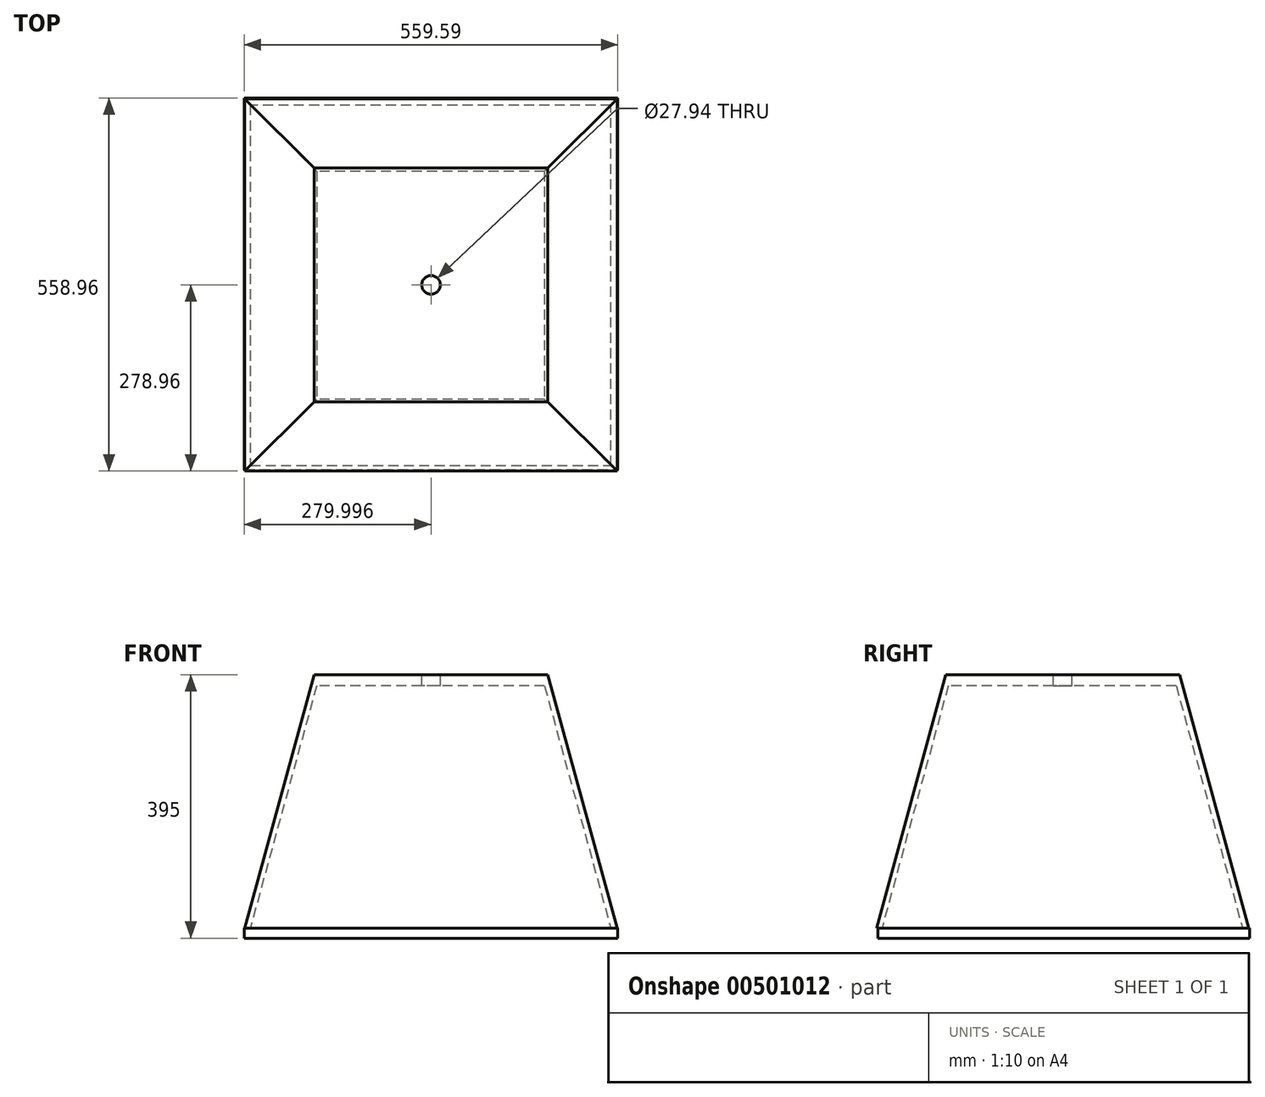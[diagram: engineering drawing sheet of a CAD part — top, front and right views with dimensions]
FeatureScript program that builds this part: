
annotation { "Feature Type Name" : "Feature", "Feature Type Description" : "" }
export const myFeature = defineFeature(function(context is Context, id is Id, definition is map)
    precondition{}
    {
        {
            var Q0;
            Q0=qCreatedBy(makeId("Right.planeOp"),FACE);
            var sketch = newSketch(context, id + "F0", { "sketchPlane" : qUnion([Q0])});
            skLineSegment(sketch, "E0.bottom", {"start": v(0, 0) * mm, "end": v(-560, 0) * mm});
            skLineSegment(sketch, "E0.top", {"start": v(0, -560) * mm, "end": v(-560, -560) * mm});
            skLineSegment(sketch, "E0.left", {"start": v(0, 0) * mm, "end": v(0, -560) * mm});
            skLineSegment(sketch, "E0.right", {"start": v(-560, 0) * mm, "end": v(-560, -560) * mm});
            skSolve(sketch);
        }
        {
            var Q0;
            Q0=qSketchRegion(id+"F0",true);
            var Q1;
            Q1=makeQuery(id+"F0.imprint","IMPRINT",FACE,{"disambiguationData":[TD([[makeQuery(id+"F0.imprint","IMPRINT",EDGE,{"derivedFrom":sQuery(id+"F0.wireOp",EDGE,"E0.bottom")}),1.0]])]});
            extrude(context, id + "F1", {"entities" : qUnion([Q0, Q1]), "depth" : 380 * mm});
        }
        {
            var Q0;
            Q0=makeQuery(id+"F1.opExtrude","CAP_EDGE",EDGE,{"disambiguationData":[OSD([sQuery(id+"F0.wireOp",EDGE,"E0.top")])],"isStart":false});
            chamfer(context, id + "F2", {"entities" : qUnion([Q0]), "chamferType" : ChamferType.OFFSET_ANGLE, "width" : 105 * mm, "oppositeDirection" : true, "angle" : 74.7 * degree, "tangentPropagation" : true});
        }
        {
            var Q0;
            Q0=makeQuery(id+"F1.opExtrude","CAP_EDGE",EDGE,{"disambiguationData":[OSD([sQuery(id+"F0.wireOp",EDGE,"E0.bottom")])],"isStart":false});
            chamfer(context, id + "F3", {"entities" : qUnion([Q0]), "chamferType" : ChamferType.OFFSET_ANGLE, "width" : 105 * mm, "oppositeDirection" : false, "angle" : 74.7 * degree, "tangentPropagation" : true});
        }
        {
            var Q0;
            Q0=makeQuery(id+"F1.opExtrude","CAP_EDGE",EDGE,{"disambiguationData":[OSD([sQuery(id+"F0.wireOp",EDGE,"E0.right")])],"isStart":false});
            chamfer(context, id + "F4", {"entities" : qUnion([Q0]), "chamferType" : ChamferType.OFFSET_ANGLE, "width" : 105 * mm, "oppositeDirection" : false, "angle" : 74.7 * degree, "tangentPropagation" : true});
        }
        {
            var Q0;
            Q0=makeQuery(id+"F1.opExtrude","CAP_EDGE",EDGE,{"disambiguationData":[OSD([sQuery(id+"F0.wireOp",EDGE,"E0.left")])],"isStart":false});
            chamfer(context, id + "F5", {"entities" : qUnion([Q0]), "chamferType" : ChamferType.OFFSET_ANGLE, "width" : 105 * mm, "oppositeDirection" : true, "angle" : 74.7 * degree, "tangentPropagation" : true});
        }
        {
            var Q0;
            Q0=makeQuery(id+"F1.opExtrude","CAP_FACE",FACE,{"disambiguationData":[OSD([sQuery(id+"F0.wireOp",EDGE,"E0.bottom"),sQuery(id+"F0.wireOp",EDGE,"E0.top"),sQuery(id+"F0.wireOp",EDGE,"E0.left"),sQuery(id+"F0.wireOp",EDGE,"E0.right")])],"isStart":false});
            var sketch = newSketch(context, id + "F6", { "sketchPlane" : qUnion([Q0])});
            skLineSegment(sketch, "E1", {"start": v(-105, -455) * mm, "end": v(-455, -455) * mm});
            skCircle(sketch, "E2", {"center": v(-280, -280) * mm, "radius": 13.97 * mm});
            skPoint(sketch, "E3.orphan", {"position": v(-105, -105) * mm});
            skSolve(sketch);
        }
        {
            var Q0;
            Q0=makeQuery(id+"F6.imprint","IMPRINT",FACE,{"disambiguationData":[TD([[makeQuery(id+"F6.imprint","IMPRINT",EDGE,{"derivedFrom":sQuery(id+"F6.wireOp",EDGE,"E2")}),1.0]])]});
            extrude(context, id + "F7", {"entities" : qUnion([Q0]), "operationType" : NewBodyOperationType.REMOVE, "oppositeDirection" : true, "depth" : 111.76 * mm});
        }
        {
            var Q0;
            Q0=makeQuery(id+"F1.opExtrude","CAP_FACE",FACE,{"disambiguationData":[OSD([sQuery(id+"F0.wireOp",EDGE,"E0.bottom"),sQuery(id+"F0.wireOp",EDGE,"E0.top"),sQuery(id+"F0.wireOp",EDGE,"E0.left"),sQuery(id+"F0.wireOp",EDGE,"E0.right")])],"isStart":false});
            var sketch = newSketch(context, id + "F8", { "sketchPlane" : qUnion([Q0])});
            skLineSegment(sketch, "E4", {"start": v(-455, -455) * mm, "end": v(-105, -455) * mm});
            skLineSegment(sketch, "E5.bottom", {"start": v(-115.62, -444.38) * mm, "end": v(-445.78, -444.38) * mm});
            skLineSegment(sketch, "E5.top", {"start": v(-115.62, -114.22) * mm, "end": v(-445.78, -114.22) * mm});
            skLineSegment(sketch, "E5.left", {"start": v(-115.62, -444.38) * mm, "end": v(-115.62, -114.22) * mm});
            skLineSegment(sketch, "E5.right", {"start": v(-445.78, -444.38) * mm, "end": v(-445.78, -114.22) * mm});
            skSolve(sketch);
        }
        {
            var Q0;
            Q0=qSketchRegion(id+"F8",true);
            var Q1;
            Q1=makeQuery(id+"F8.imprint","IMPRINT",FACE,{"disambiguationData":[TD([[makeQuery(id+"F8.imprint","IMPRINT",EDGE,{"derivedFrom":sQuery(id+"F8.wireOp",EDGE,"E5.bottom")}),-1.0]])]});
            extrude(context, id + "F9", {"entities" : qUnion([Q0, Q1]), "operationType" : NewBodyOperationType.REMOVE, "oppositeDirection" : true, "depth" : 505.46 * mm});
        }
        {
            var Q0;
            Q0=makeQuery(id+"F9.boolean.opBoolean","COPY",FACE,{"derivedFrom":makeQuery(id+"F9.opExtrude","SWEPT_FACE",FACE,{"disambiguationData":[OSD([sQuery(id+"F8.wireOp",EDGE,"E5.bottom")])]})});
            var sketch = newSketch(context, id + "F10", { "sketchPlane" : qUnion([Q0])});
            skLineSegment(sketch, "E6.bottom", {"start": v(380, -115.62) * mm, "end": v(363.2, -115.62) * mm});
            skLineSegment(sketch, "E6.top", {"start": v(380, -445.78) * mm, "end": v(363.2, -445.78) * mm});
            skLineSegment(sketch, "E6.left", {"start": v(380, -115.62) * mm, "end": v(380, -445.78) * mm});
            skLineSegment(sketch, "E6.right", {"start": v(363.2, -115.62) * mm, "end": v(363.2, -445.78) * mm});
            skSolve(sketch);
        }
        {
            var Q0;
            Q0=qSketchRegion(id+"F10",true);
            extrude(context, id + "F11", {"entities" : qUnion([Q0]), "operationType" : NewBodyOperationType.ADD, "depth" : 332.5 * mm});
        }
        {
            var Q0;
            Q0=makeQuery(id+"F11.boolean.opBoolean","MERGE",FACE,{"derivedFrom":[makeQuery(id+"F1.opExtrude","CAP_FACE",FACE,{"disambiguationData":[OSD([sQuery(id+"F0.wireOp",EDGE,"E0.bottom"),sQuery(id+"F0.wireOp",EDGE,"E0.top"),sQuery(id+"F0.wireOp",EDGE,"E0.left"),sQuery(id+"F0.wireOp",EDGE,"E0.right")])],"isStart":false}),makeQuery(id+"F11.opExtrude","SWEPT_FACE",FACE,{"disambiguationData":[OSD([sQuery(id+"F10.wireOp",EDGE,"E6.left")])]})]});
            var sketch = newSketch(context, id + "F12", { "sketchPlane" : qUnion([Q0])});
            skLineSegment(sketch, "E7", {"start": v(-455, -455) * mm, "end": v(-105, -455) * mm});
            skCircle(sketch, "E8", {"center": v(-280, -280) * mm, "radius": 13.97 * mm});
            skPoint(sketch, "E9.orphan", {"position": v(-105, -105) * mm});
            skSolve(sketch);
        }
        {
            var Q0;
            Q0=makeQuery(id+"F12.imprint","IMPRINT",FACE,{"disambiguationData":[TD([[makeQuery(id+"F12.imprint","IMPRINT",EDGE,{"derivedFrom":sQuery(id+"F12.wireOp",EDGE,"E8")}),1.0]])]});
            extrude(context, id + "F13", {"entities" : qUnion([Q0]), "operationType" : NewBodyOperationType.REMOVE, "oppositeDirection" : true, "depth" : 237.74 * mm});
        }
        {
            var Q0;
            Q0=makeQuery(id+"F9.boolean.opBoolean","INTERSECT",EDGE,{"derivedFrom":[makeQuery(id+"F1.opExtrude","CAP_FACE",FACE,{"disambiguationData":[OSD([sQuery(id+"F0.wireOp",EDGE,"E0.bottom"),sQuery(id+"F0.wireOp",EDGE,"E0.top"),sQuery(id+"F0.wireOp",EDGE,"E0.left"),sQuery(id+"F0.wireOp",EDGE,"E0.right")])],"isStart":true}),makeQuery(id+"F9.opExtrude","SWEPT_FACE",FACE,{"disambiguationData":[OSD([sQuery(id+"F8.wireOp",EDGE,"E5.left")])]})]});
            chamfer(context, id + "F14", {"entities" : qUnion([Q0]), "chamferType" : ChamferType.OFFSET_ANGLE, "width" : 105 * mm, "oppositeDirection" : false, "angle" : 74.7 * degree, "tangentPropagation" : true});
        }
        {
            var Q0;
            Q0=makeQuery(id+"F9.boolean.opBoolean","INTERSECT",EDGE,{"derivedFrom":[makeQuery(id+"F1.opExtrude","CAP_FACE",FACE,{"disambiguationData":[OSD([sQuery(id+"F0.wireOp",EDGE,"E0.bottom"),sQuery(id+"F0.wireOp",EDGE,"E0.top"),sQuery(id+"F0.wireOp",EDGE,"E0.left"),sQuery(id+"F0.wireOp",EDGE,"E0.right")])],"isStart":true}),makeQuery(id+"F9.opExtrude","SWEPT_FACE",FACE,{"disambiguationData":[OSD([sQuery(id+"F8.wireOp",EDGE,"E5.right")])]})]});
            chamfer(context, id + "F15", {"entities" : qUnion([Q0]), "chamferType" : ChamferType.OFFSET_ANGLE, "width" : 105 * mm, "oppositeDirection" : true, "angle" : 74.7 * degree, "tangentPropagation" : true});
        }
        {
            var Q0;
            Q0=makeQuery(id+"F9.boolean.opBoolean","INTERSECT",EDGE,{"derivedFrom":[makeQuery(id+"F1.opExtrude","CAP_FACE",FACE,{"disambiguationData":[OSD([sQuery(id+"F0.wireOp",EDGE,"E0.bottom"),sQuery(id+"F0.wireOp",EDGE,"E0.top"),sQuery(id+"F0.wireOp",EDGE,"E0.left"),sQuery(id+"F0.wireOp",EDGE,"E0.right")])],"isStart":true}),makeQuery(id+"F9.opExtrude","SWEPT_FACE",FACE,{"disambiguationData":[OSD([sQuery(id+"F8.wireOp",EDGE,"E5.bottom")])]})]});
            chamfer(context, id + "F16", {"entities" : qUnion([Q0]), "chamferType" : ChamferType.OFFSET_ANGLE, "width" : 105 * mm, "oppositeDirection" : true, "angle" : 74.7 * degree, "tangentPropagation" : true});
        }
        {
            var Q0;
            Q0=makeQuery(id+"F9.boolean.opBoolean","INTERSECT",EDGE,{"derivedFrom":[makeQuery(id+"F1.opExtrude","CAP_FACE",FACE,{"disambiguationData":[OSD([sQuery(id+"F0.wireOp",EDGE,"E0.bottom"),sQuery(id+"F0.wireOp",EDGE,"E0.top"),sQuery(id+"F0.wireOp",EDGE,"E0.left"),sQuery(id+"F0.wireOp",EDGE,"E0.right")])],"isStart":true}),makeQuery(id+"F9.opExtrude","SWEPT_FACE",FACE,{"disambiguationData":[OSD([sQuery(id+"F8.wireOp",EDGE,"E5.top")])]})]});
            chamfer(context, id + "F17", {"entities" : qUnion([Q0]), "chamferType" : ChamferType.OFFSET_ANGLE, "width" : 105 * mm, "oppositeDirection" : false, "angle" : 74.7 * degree, "tangentPropagation" : true});
        }
        {
            var Q0;
            Q0=makeQuery(id+"F1.opExtrude","CAP_FACE",FACE,{"disambiguationData":[OSD([sQuery(id+"F0.wireOp",EDGE,"E0.bottom"),sQuery(id+"F0.wireOp",EDGE,"E0.top"),sQuery(id+"F0.wireOp",EDGE,"E0.left"),sQuery(id+"F0.wireOp",EDGE,"E0.right")])],"isStart":true});
            var sketch = newSketch(context, id + "F18", { "sketchPlane" : qUnion([Q0])});
            skLineSegment(sketch, "E10.bottom", {"start": v(10.62, -9.22) * mm, "end": v(550.78, -9.22) * mm});
            skLineSegment(sketch, "E10.top", {"start": v(10.62, -549.38) * mm, "end": v(550.78, -549.38) * mm});
            skLineSegment(sketch, "E10.left", {"start": v(10.62, -9.22) * mm, "end": v(10.62, -549.38) * mm});
            skLineSegment(sketch, "E10.right", {"start": v(550.78, -9.22) * mm, "end": v(550.78, -549.38) * mm});
            skSolve(sketch);
        }
        {
            var Q0;
            Q0=makeQuery(id+"F18.imprint","IMPRINT",FACE,{"disambiguationData":[TD([[makeQuery(id+"F18.imprint","IMPRINT",EDGE,{"derivedFrom":sQuery(id+"F18.wireOp",EDGE,"E10.bottom")}),1.0]])]});
            var sketch = newSketch(context, id + "F19", { "sketchPlane" : qUnion([Q0])});
            skLineSegment(sketch, "E11.bottom", {"start": v(0, 0) * mm, "end": v(556.78, 0) * mm});
            skLineSegment(sketch, "E11.top", {"start": v(0, -559.6) * mm, "end": v(556.78, -559.6) * mm});
            skLineSegment(sketch, "E11.left", {"start": v(0, 0) * mm, "end": v(0, -559.6) * mm});
            skLineSegment(sketch, "E11.right", {"start": v(556.78, 0) * mm, "end": v(556.78, -559.6) * mm});
            skSolve(sketch);
        }
        {
            var Q0;
            Q0 = qSketchRegion(id + "F19", true);
            extrude(context, id + "F20", {"entities" : qUnion([Q0]), "operationType" : NewBodyOperationType.ADD, "depth" : 15 * mm});
        }
        {
            var Q0;
            Q0=makeQuery(id+"F1.opExtrude","SWEPT_BODY",BODY,{"disambiguationData":[OSD([sQuery(id+"F0.wireOp",EDGE,"E0.bottom"),sQuery(id+"F0.wireOp",EDGE,"E0.top"),sQuery(id+"F0.wireOp",EDGE,"E0.left"),sQuery(id+"F0.wireOp",EDGE,"E0.right")])]});
            var Q1;
            Q1=makeQuery(id+"F20.opExtrude","CAP_EDGE",EDGE,{"disambiguationData":[OSD([sQuery(id+"F19.wireOp",EDGE,"E11.top")])],"isStart":false});
            transform(context, id + "F21", {"entities" : qUnion([Q0]), "transformType" : TransformType.ROTATION, "transformAxis" : qUnion([Q1]), "angle" : 90 * degree, "makeCopy" : false});
        }
    });
